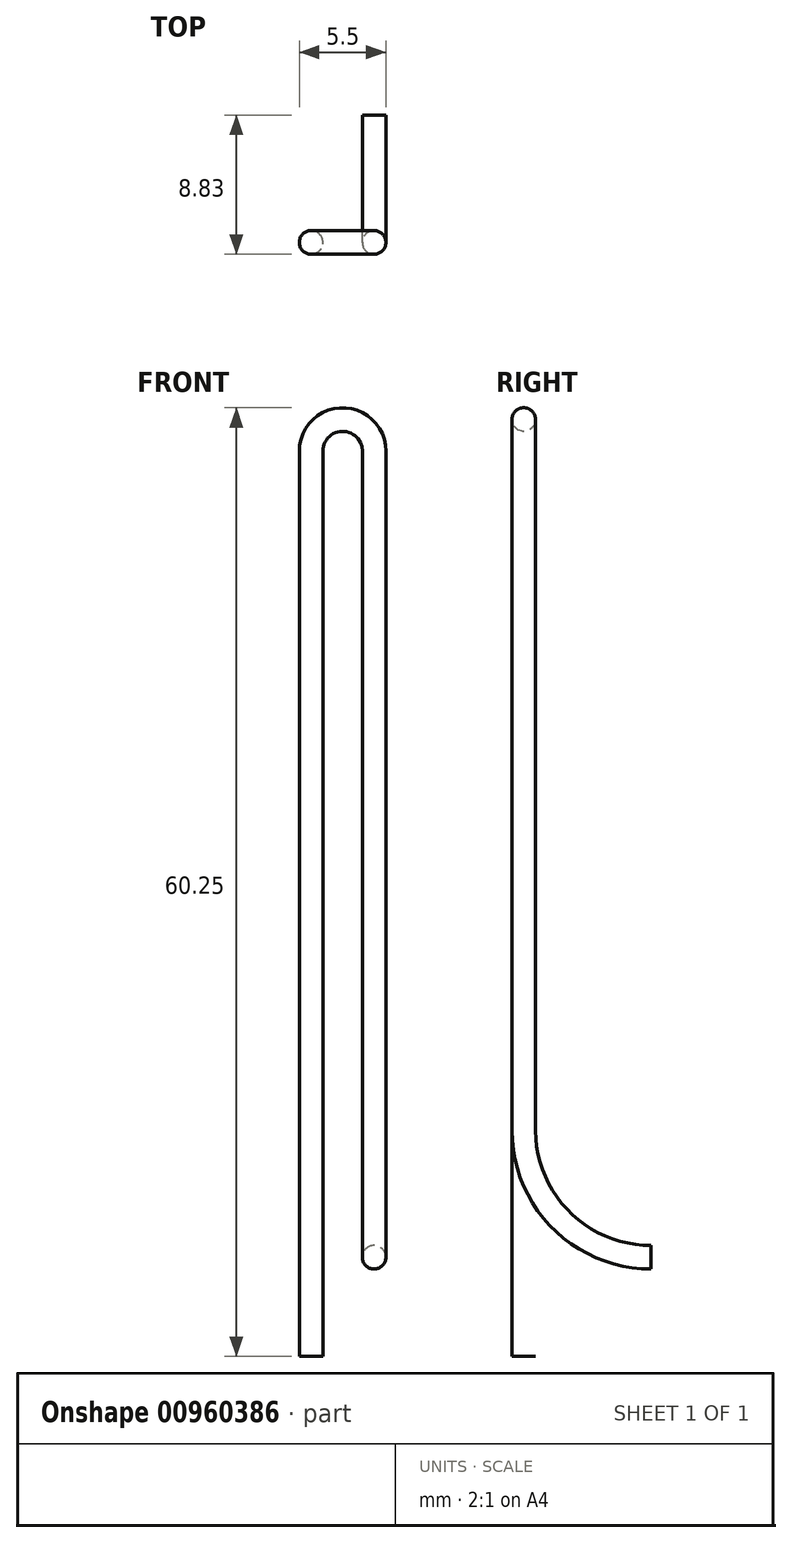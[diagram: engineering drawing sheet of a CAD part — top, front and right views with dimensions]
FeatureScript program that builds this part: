
annotation { "Feature Type Name" : "Feature", "Feature Type Description" : "" }
export const myFeature = defineFeature(function(context is Context, id is Id, definition is map)
    precondition{}
    {
        {
            var Q0;
            Q0=qCreatedBy(makeId("Front.planeOp"),FACE);
            var sketch = newSketch(context, id + "F0", { "sketchPlane" : qUnion([Q0])});
            skLineSegment(sketch, "E0", {"start": v(0, 0) * mm, "end": v(0, 43.18) * mm});
            skArc(sketch, "E1", {"start": v(0, 43.18) * mm, "mid": v(-2, 45.18) * mm, "end": v(-4, 43.18) * mm});
            skLineSegment(sketch, "E2", {"start": v(-4, 43.18) * mm, "end": v(-4, 0) * mm});
            skLineSegment(sketch, "E3", {"start": v(-4, 0) * mm, "end": v(-4, -14.32) * mm});
            skSolve(sketch);
        }
        {
            var Q0;
            Q0=qCreatedBy(makeId("Right.planeOp"),FACE);
            var sketch = newSketch(context, id + "F1", { "sketchPlane" : qUnion([Q0])});
            skArc(sketch, "E4", {"start": v(0, 0) * mm, "mid": v(2.39, -5.68) * mm, "end": v(8.08, -8.03) * mm});
            skSolve(sketch);
        }
        {
            var Q0;
            Q0=qCreatedBy(makeId("Top.planeOp"),FACE);
            var sketch = newSketch(context, id + "F2", { "sketchPlane" : qUnion([Q0])});
            skCircle(sketch, "E5", {"center": v(0, 0) * mm, "radius": 0.75 * mm});
            skSolve(sketch);
        }
        {
            var Q0;
            Q0=makeQuery(id+"F2.imprint","IMPRINT",FACE,{"disambiguationData":[TD([[makeQuery(id+"F2.imprint","IMPRINT",EDGE,{"derivedFrom":sQuery(id+"F2.wireOp",EDGE,"E5")}),1.0]])]});
            var Q1;
            Q1=sQuery(id+"F0.wireOp",EDGE,"E0");
            var Q2;
            Q2=sQuery(id+"F1.wireOp",EDGE,"E4");
            var Q3;
            Q3=sQuery(id+"F0.wireOp",EDGE,"E1");
            var Q4;
            Q4=sQuery(id+"F0.wireOp",EDGE,"E2");
            var Q5;
            Q5=sQuery(id+"F0.wireOp",EDGE,"E3");
            sweep(context, id + "F3", {"profiles" : qUnion([Q0]), "path" : qUnion([Q1, Q2, Q3, Q4, Q5])});
        }
    });
